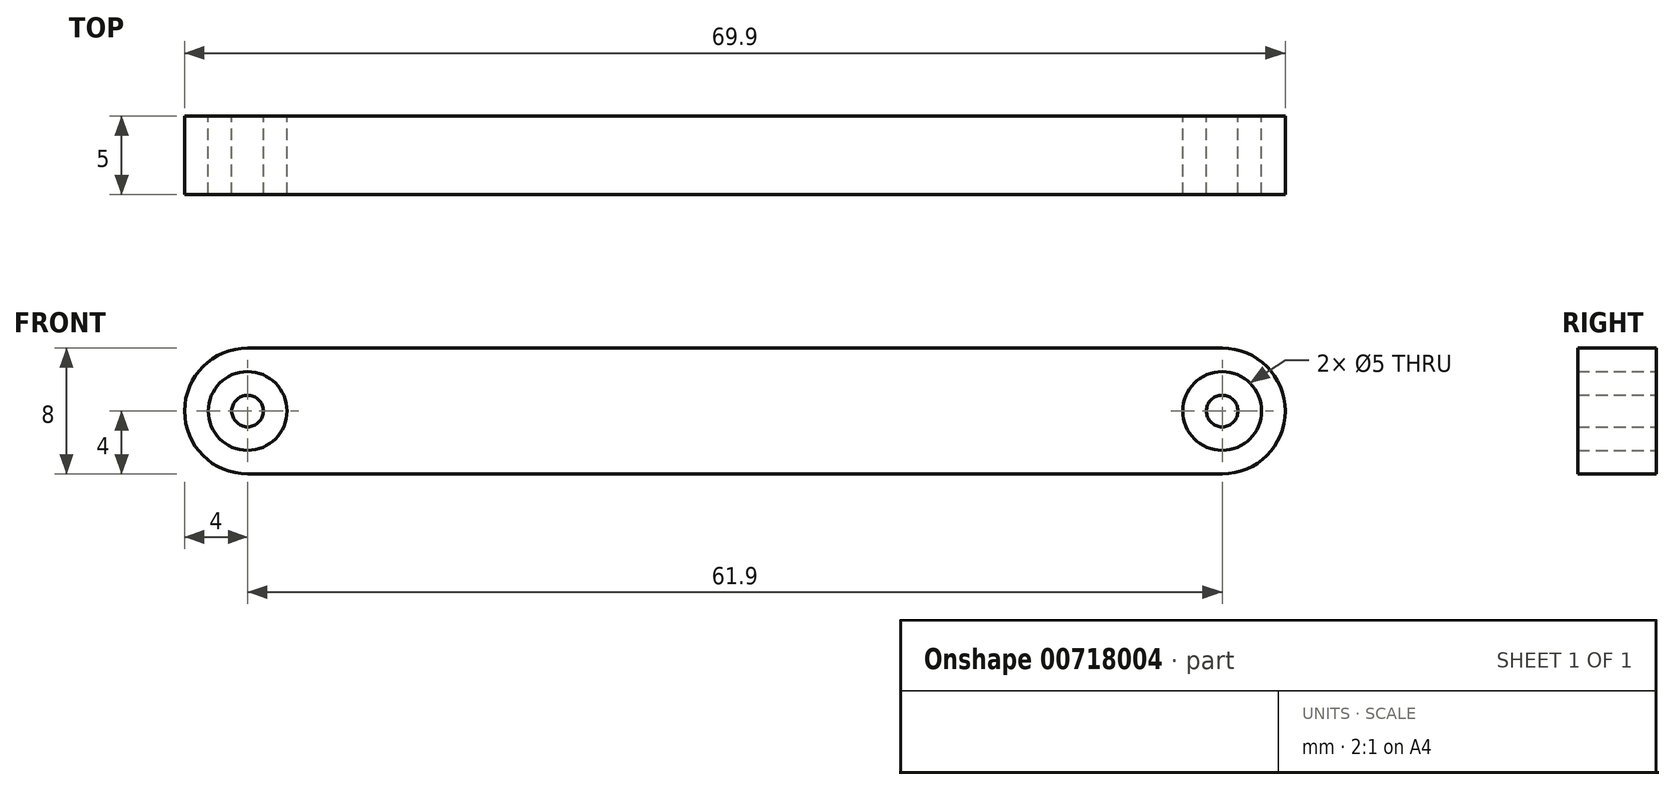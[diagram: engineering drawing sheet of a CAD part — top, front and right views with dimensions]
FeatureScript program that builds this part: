
annotation { "Feature Type Name" : "Feature", "Feature Type Description" : "" }
export const myFeature = defineFeature(function(context is Context, id is Id, definition is map)
    precondition{}
    {
        {
            var Q0;
            Q0=qCreatedBy(makeId("Front.planeOp"),FACE);
            var sketch = newSketch(context, id + "F0", { "sketchPlane" : qUnion([Q0])});
            skCircle(sketch, "E0", {"center": v(0, 0) * mm, "radius": 2.5 * mm});
            skCircle(sketch, "E1", {"center": v(0, 0) * mm, "radius": 1 * mm});
            skCircle(sketch, "E2", {"center": v(0, 0) * mm, "radius": 4 * mm});
            skCircle(sketch, "E3", {"center": v(61.9, 0) * mm, "radius": 4 * mm});
            skCircle(sketch, "E4", {"center": v(61.9, 0) * mm, "radius": 2.5 * mm});
            skCircle(sketch, "E5", {"center": v(61.9, 0) * mm, "radius": 1 * mm});
            skLineSegment(sketch, "E6", {"start": v(0, -4) * mm, "end": v(61.9, -4) * mm});
            skLineSegment(sketch, "E7", {"start": v(0, 4) * mm, "end": v(61.9, 4) * mm});
            skSolve(sketch);
        }
        {
            var Q0;
            Q0 = qSketchRegion(id + "F0", true);
            var Q1;
            Q1=makeQuery(id+"F0.imprint","IMPRINT",FACE,{"disambiguationData":[TD([[makeQuery(id+"F0.imprint","IMPRINT",EDGE,{"derivedFrom":sQuery(id+"F0.wireOp",EDGE,"E1")}),1.0]])]});
            var Q2;
            Q2=makeQuery(id+"F0.imprint","IMPRINT",FACE,{"disambiguationData":[TD([[makeQuery(id+"F0.imprint","IMPRINT",EDGE,{"derivedFrom":sQuery(id+"F0.wireOp",EDGE,"E5")}),1.0]])]});
            extrude(context, id + "F1", {"entities" : qUnion([Q0, Q1, Q2]), "depth" : 5 * mm, "offsetDistance" : 25.4 * mm});
        }
    });
